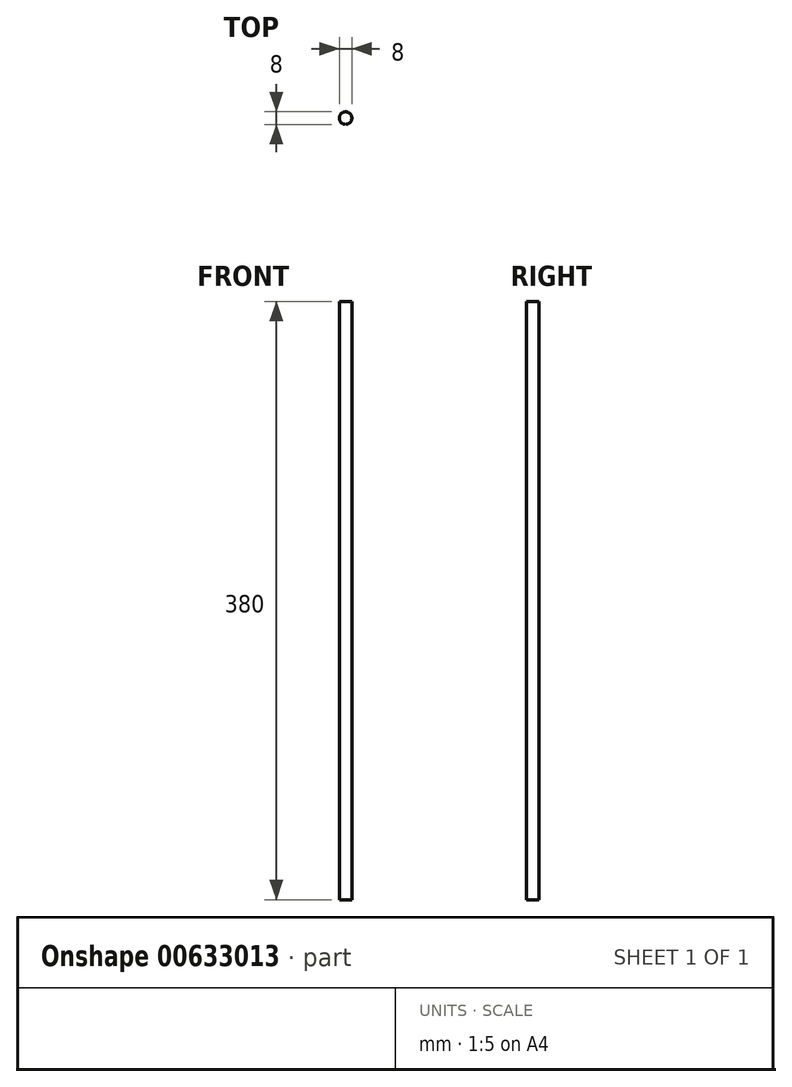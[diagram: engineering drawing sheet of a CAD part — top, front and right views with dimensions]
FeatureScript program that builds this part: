
annotation { "Feature Type Name" : "Feature", "Feature Type Description" : "" }
export const myFeature = defineFeature(function(context is Context, id is Id, definition is map)
    precondition{}
    {
        {
            var Q0;
            Q0=qCreatedBy(makeId("Top.planeOp"),FACE);
            var sketch = newSketch(context, id + "F0", { "sketchPlane" : qUnion([Q0])});
            skCircle(sketch, "E0", {"center": v(0, 0) * mm, "radius": 4 * mm});
            skSolve(sketch);
        }
        {
            var Q0;
            Q0=qSketchRegion(id+"F0",true);
            extrude(context, id + "F1", {"entities" : qUnion([Q0]), "depth" : 380 * mm});
        }
    });
